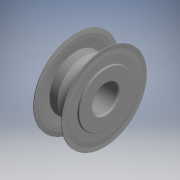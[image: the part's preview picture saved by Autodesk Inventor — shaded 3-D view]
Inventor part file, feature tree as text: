
AUTODESK INVENTOR PART (.ipt)
format: ipt  version: 2017.3 (Build 213256000, 256)  size: 189,440 bytes
history: native  units: mm (DEFAULTED — no unit token found)
features: revolve x3, sketch x3
ambient origin geometry x8: Origin, YZ Plane, XZ Plane, XY Plane, X Axis, Y Axis, Z Axis, Center Point
bodies: Solid1 (feature_tree)
feature tree (6):
  revolve  "Revolution1"  Angle=360.0deg
  revolve  "Revolution2"  [1 undecoded]
  revolve  "Revolution3"  [1 undecoded]
  sketch  "Sketch_62"  dims[d0=360.0deg d1=360.0deg]
  sketch  "Sketch_63"  dims[d2=360.0deg]
  sketch  "Sketch_65"
note: 2 required parameter values undecoded (feature->parameter linkage not recoverable at this tier; creation-order binding heuristic only, values carry confidence <= 0.55)
